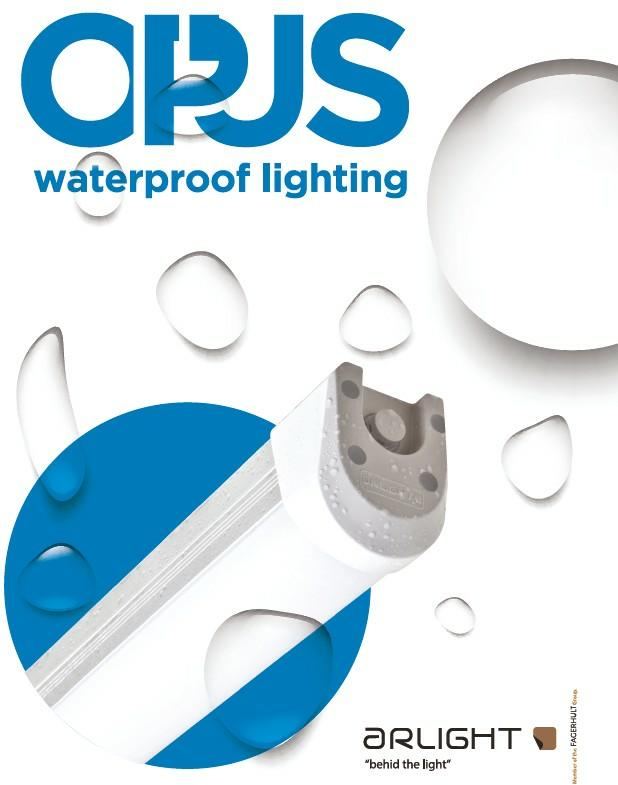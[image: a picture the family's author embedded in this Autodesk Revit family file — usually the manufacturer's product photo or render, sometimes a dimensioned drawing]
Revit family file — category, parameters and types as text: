
# Revit family: E 0900 PUS
name_source: partatom
category: Lighting Fixtures
revit_build: Autodesk Revit 2017 (Build: 20160225_1515(x64)
units: mm (PartAtom-declared; Revit-internal decimal feet)

## family parameters
Cut with Voids When Loaded = No
Host = Face
Light Source = Yes
Part Type = Normal
Room Calculation Point = No
Round Connector Dimension = Use Diameter
Shared = No

## types (8) — shared parameters
Color Filter = 16777215
Default Elevation = 1219 mm
Description = Double Connector
Dimming Lamp Color Temperature Shift = <None>
Emit Shape Visible in Rendering = No
Emit from Rectangle Length = 850 mm  [stored 2.78871 ft]
Emit from Rectangle Width = 55 mm  [stored 0.180446 ft]
Lamp = LED
Manufacturer = ARLIGHT AYDINLATMA
Model = E 0900 PUS (CK)
Photometric Web File = E 0900 PUS-38W-4K(SK).IES
Tilt Angle = -90.00°
Type Comments = Waterproof Lighting
Type Image = OPUS.jpg
URL = http://www.arlight.net

## per-type parameters (varying)
| type | Apparent Load | Wattage Comments |
| EPUS.900.38.40.TK | 38 VA | 38W |
| EPUS.900.38.40.CK | 38 VA | 38W |
| EPUS.900.27.40.TK | 27 VA | 27W |
| EPUS.900.27.40.CK | 27 VA | 27W |
| EPUS.900.27.40.TR | 27 VA | 27W |
| EPUS.900.38.40.TR | 38 VA | 38W |
| EPUS.900.27.40.CR | 27 VA | 27W |
| EPUS.900.38.40.CR | 38 VA | 38W |

note: [stored X ft] marks values corroborated as IEEE doubles in the binary element streams (Revit-internal decimal feet)

## geometry (parser evidence)
native form markers: Sweep x3
no freeform markers — native parametric forms only
